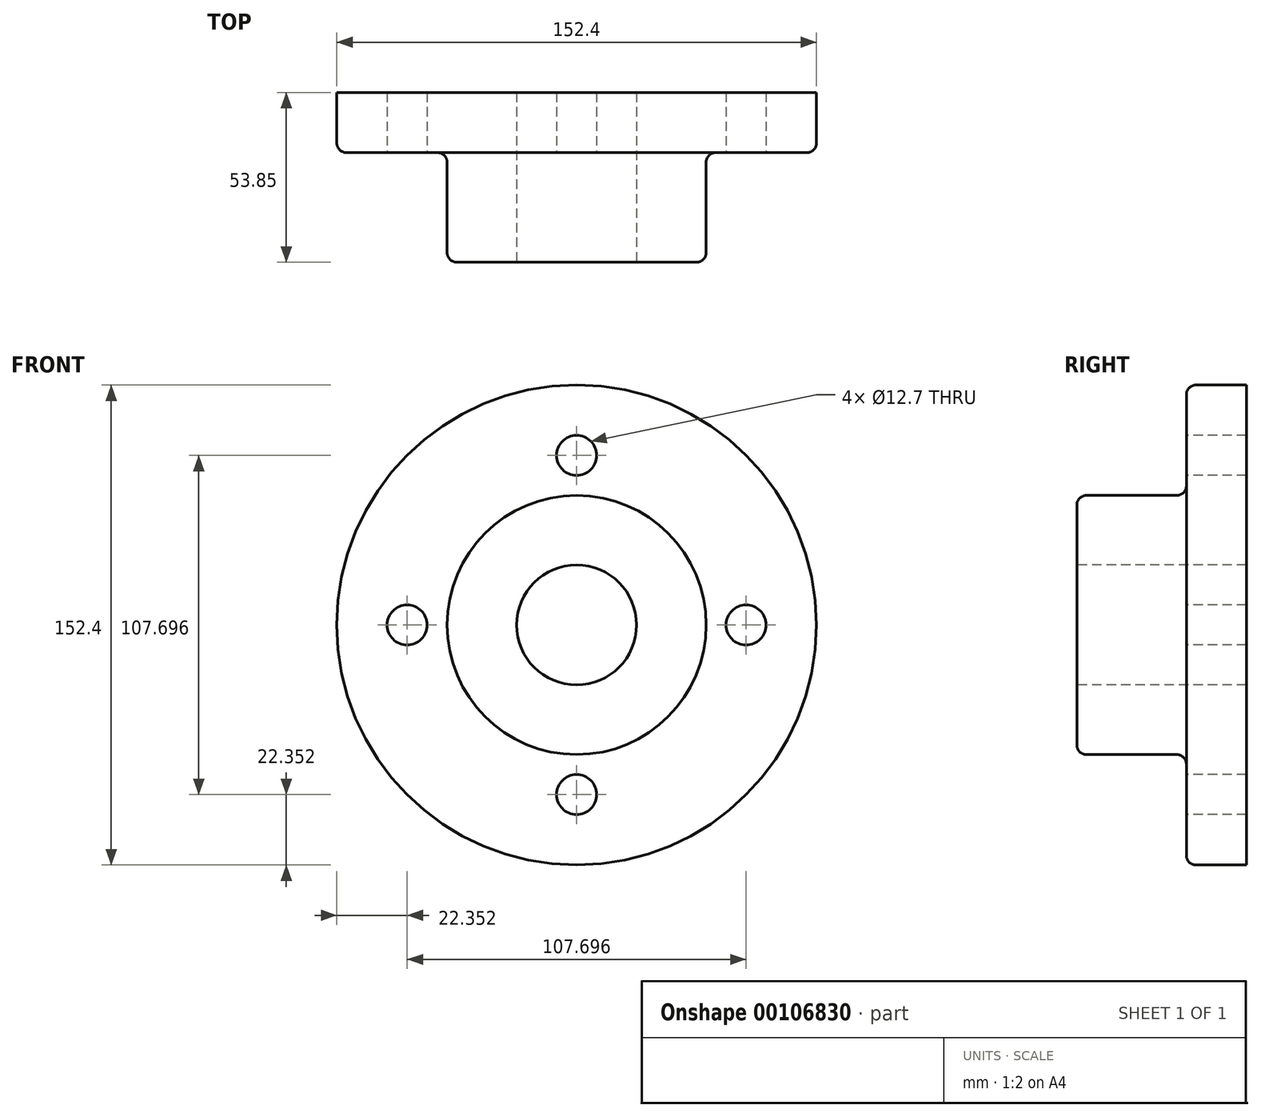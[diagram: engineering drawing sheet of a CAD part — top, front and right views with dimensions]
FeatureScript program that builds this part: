
annotation { "Feature Type Name" : "Feature", "Feature Type Description" : "" }
export const myFeature = defineFeature(function(context is Context, id is Id, definition is map)
    precondition{}
    {
        {
            var Q0;
            Q0=qCreatedBy(makeId("Right.planeOp"),FACE);
            var sketch = newSketch(context, id + "F0", { "sketchPlane" : qUnion([Q0])});
            skLineSegment(sketch, "E0", {"start": v(53.85, 19.05) * mm, "end": v(53.85, 76.2) * mm});
            skLineSegment(sketch, "E1", {"start": v(53.85, 76.2) * mm, "end": v(37.85, 76.2) * mm});
            skLineSegment(sketch, "E2", {"start": v(34.8, 73.15) * mm, "end": v(34.8, 44.2) * mm});
            skLineSegment(sketch, "E3", {"start": v(31.75, 41.15) * mm, "end": v(3.05, 41.15) * mm});
            skLineSegment(sketch, "E4", {"start": v(0, 38.1) * mm, "end": v(0, 19.05) * mm});
            skPoint(sketch, "E5.visualSharp", {"position": v(0, 41.15) * mm});
            skArc(sketch, "E5.filletArc", {"start": v(3.05, 41.15) * mm, "mid": v(0.9, 40.26) * mm, "end": v(0, 38.1) * mm});
            skPoint(sketch, "E6.visualSharp", {"position": v(34.8, 76.2) * mm});
            skArc(sketch, "E6.filletArc", {"start": v(37.85, 76.2) * mm, "mid": v(35.7, 75.3) * mm, "end": v(34.8, 73.15) * mm});
            skPoint(sketch, "E7.visualSharp", {"position": v(34.8, 41.15) * mm});
            skArc(sketch, "E7.filletArc", {"start": v(31.75, 41.15) * mm, "mid": v(33.9, 42.04) * mm, "end": v(34.8, 44.2) * mm});
            skLineSegment(sketch, "E8", {"start": v(0, 19.05) * mm, "end": v(53.85, 19.05) * mm});
            skPoint(sketch, "E9.orphan", {"position": v(0, 0) * mm});
            skLineSegment(sketch, "E10", {"start": v(0, 0) * mm, "end": v(70.93, 0) * mm, "construction": true});
            skSolve(sketch);
        }
        {
            var Q0;
            Q0=makeQuery(id+"F0.imprint","IMPRINT",FACE,{"disambiguationData":[TD([[makeQuery(id+"F0.imprint","IMPRINT",EDGE,{"derivedFrom":sQuery(id+"F0.wireOp",EDGE,"E0")}),1.0]])]});
            var Q1;
            Q1=sQuery(id+"F0.wireOp",EDGE,"E10");
            revolve(context, id + "F1", {"entities" : qUnion([Q0]), "axis" : qUnion([Q1]), "revolveType" : RevolveType.FULL});
        }
        {
            var Q0;
            Q0=makeQuery(id+"F1.opRevolve","SWEPT_FACE",FACE,{"disambiguationData":[OSD([sQuery(id+"F0.wireOp",EDGE,"E2")])]});
            var sketch = newSketch(context, id + "F2", { "sketchPlane" : qUnion([Q0])});
            skCircle(sketch, "E11", {"center": v(0, 0) * mm, "radius": 53.85 * mm, "construction": true});
            skCircle(sketch, "E12", {"center": v(0, -53.85) * mm, "radius": 6.35 * mm});
            skCircle(sketch, "E13", {"center": v(53.85, 0) * mm, "radius": 6.35 * mm});
            skCircle(sketch, "E14", {"center": v(0, 53.85) * mm, "radius": 6.35 * mm});
            skCircle(sketch, "E15", {"center": v(-53.85, 0) * mm, "radius": 6.35 * mm});
            skSolve(sketch);
        }
        {
            var Q0;
            Q0=makeQuery(id+"F2.imprint","IMPRINT",FACE,{"disambiguationData":[TD([[makeQuery(id+"F2.imprint","IMPRINT",EDGE,{"derivedFrom":sQuery(id+"F2.wireOp",EDGE,"E14")}),1.0]])]});
            var Q1;
            Q1=makeQuery(id+"F2.imprint","IMPRINT",FACE,{"disambiguationData":[TD([[makeQuery(id+"F2.imprint","IMPRINT",EDGE,{"derivedFrom":sQuery(id+"F2.wireOp",EDGE,"E13")}),1.0]])]});
            var Q2;
            Q2=makeQuery(id+"F2.imprint","IMPRINT",FACE,{"disambiguationData":[TD([[makeQuery(id+"F2.imprint","IMPRINT",EDGE,{"derivedFrom":sQuery(id+"F2.wireOp",EDGE,"E12")}),1.0]])]});
            var Q3;
            Q3=makeQuery(id+"F2.imprint","IMPRINT",FACE,{"disambiguationData":[TD([[makeQuery(id+"F2.imprint","IMPRINT",EDGE,{"derivedFrom":sQuery(id+"F2.wireOp",EDGE,"E15")}),1.0]])]});
            extrude(context, id + "F3", {"entities" : qUnion([Q0, Q1, Q2, Q3]), "operationType" : NewBodyOperationType.REMOVE, "endBound" : BoundingType.THROUGH_ALL, "oppositeDirection" : true, "depth" : 25.4 * mm});
        }
    });
